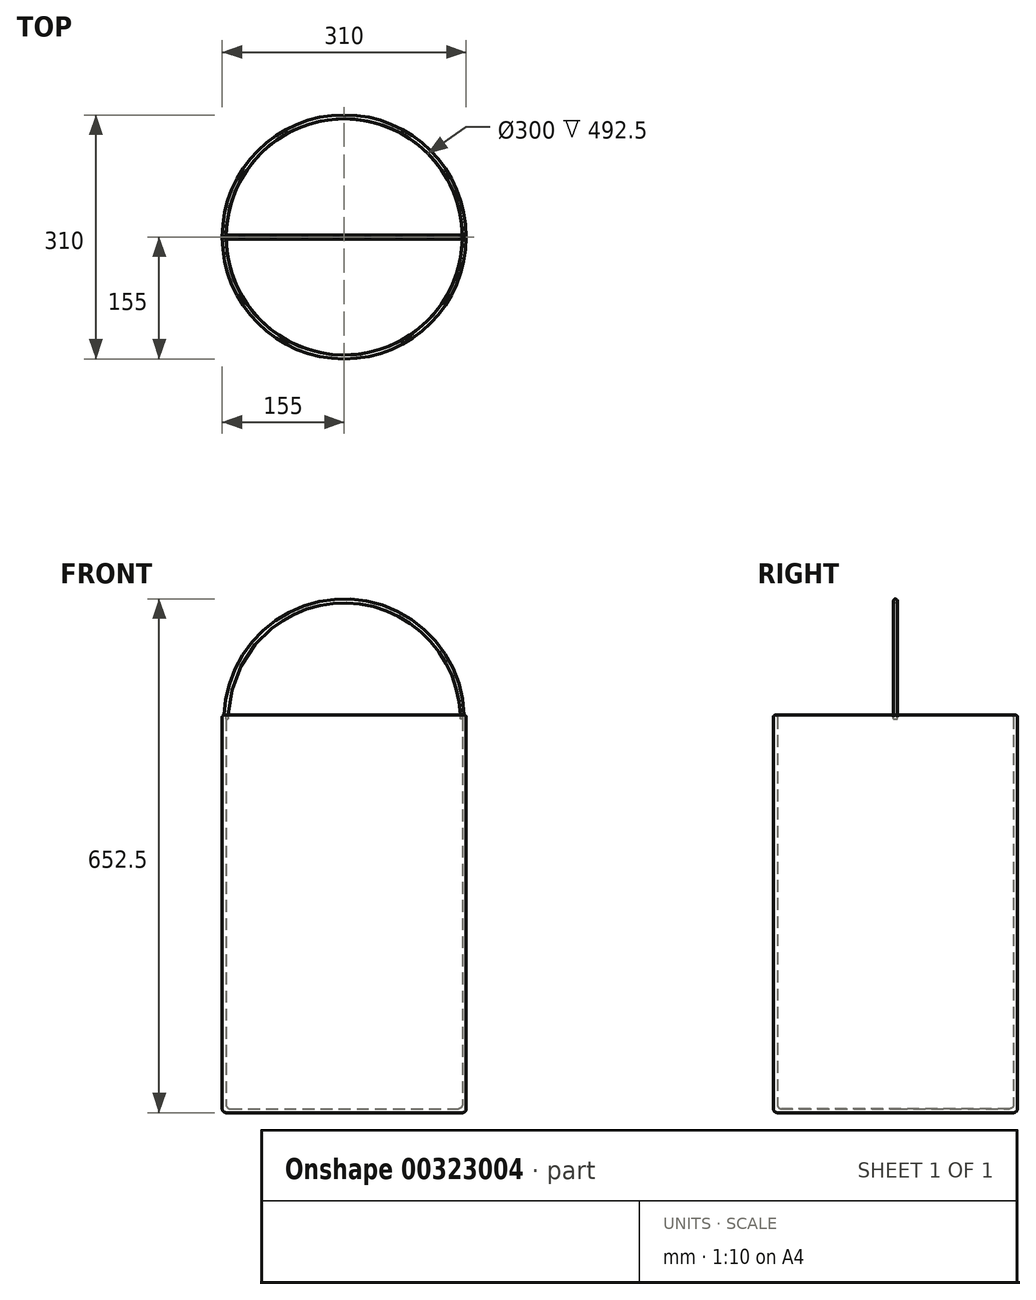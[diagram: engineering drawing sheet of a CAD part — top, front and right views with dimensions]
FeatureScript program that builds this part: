
annotation { "Feature Type Name" : "Feature", "Feature Type Description" : "" }
export const myFeature = defineFeature(function(context is Context, id is Id, definition is map)
    precondition{}
    {
        {
            var Q0;
            Q0=qCreatedBy(makeId("Front.planeOp"),FACE);
            var sketch = newSketch(context, id + "F0", { "sketchPlane" : qUnion([Q0])});
            skLineSegment(sketch, "E0", {"start": v(0, 0) * mm, "end": v(0, 5) * mm});
            skLineSegment(sketch, "E1", {"start": v(0, 0) * mm, "end": v(150, 0) * mm});
            skLineSegment(sketch, "E2", {"start": v(0, 5) * mm, "end": v(145, 5) * mm});
            skLineSegment(sketch, "E3", {"start": v(150, 10) * mm, "end": v(150, 502.5) * mm});
            skLineSegment(sketch, "E4", {"start": v(152.5, 505) * mm, "end": v(152.5, 505) * mm});
            skLineSegment(sketch, "E5", {"start": v(155, 502.5) * mm, "end": v(155, 5) * mm});
            skPoint(sketch, "E6.visualSharp", {"position": v(150, 5) * mm});
            skArc(sketch, "E6.filletArc", {"start": v(145, 5) * mm, "mid": v(148.54, 6.46) * mm, "end": v(150, 10) * mm});
            skPoint(sketch, "E7.visualSharp", {"position": v(155, 0) * mm});
            skArc(sketch, "E7.filletArc", {"start": v(150, 0) * mm, "mid": v(153.54, 1.46) * mm, "end": v(155, 5) * mm});
            skPoint(sketch, "E8.visualSharp", {"position": v(150, 505) * mm});
            skArc(sketch, "E8.filletArc", {"start": v(152.5, 505) * mm, "mid": v(150.73, 504.27) * mm, "end": v(150, 502.5) * mm});
            skPoint(sketch, "E9.visualSharp", {"position": v(155, 505) * mm});
            skArc(sketch, "E9.filletArc", {"start": v(155, 502.5) * mm, "mid": v(154.27, 504.27) * mm, "end": v(152.5, 505) * mm});
            skSolve(sketch);
        }
        {
            var Q0;
            Q0 = qSketchRegion(id + "F0", true);
            var Q1;
            Q1=sQuery(id+"F0.wireOp",EDGE,"E0");
            revolve(context, id + "F1", {"entities" : qUnion([Q0]), "axis" : qUnion([Q1]), "revolveType" : RevolveType.FULL});
        }
        {
            var Q0;
            Q0=qCreatedBy(makeId("Top.planeOp"),FACE);
            cPlane(context, id + "F2", {"entities" : qUnion([Q0]), "cplaneType" : CPlaneType.OFFSET, "offset" : 500 * mm, "width" : 150 * mm, "height" : 150 * mm});
        }
        {
            var Q0;
            Q0=makeQuery(id+"F1.opRevolve","SWEPT_EDGE",EDGE,{"disambiguationData":[OSD([sQuery(id+"F0.wireOp",EDGE,"E3"),sQuery(id+"F0.wireOp",EDGE,"E8.filletArc")])]});
            cPlane(context, id + "F3", {"entities" : qUnion([Q0]), "cplaneType" : CPlaneType.LINE_ANGLE, "offset" : 25 * mm, "angle" : 270 * degree, "width" : 150 * mm, "height" : 150 * mm});
        }
        {
            var Q0;
            Q0=qCreatedBy(id+"F2.planeOp",FACE);
            var sketch = newSketch(context, id + "F4", { "sketchPlane" : qUnion([Q0])});
            skLineSegment(sketch, "E10", {"start": v(0, 0) * mm, "end": v(0, 63.06) * mm});
            skSolve(sketch);
        }
        {
            var Q0;
            Q0=qCreatedBy(id+"F2.planeOp",FACE);
            var sketch = newSketch(context, id + "F5", { "sketchPlane" : qUnion([Q0])});
            skCircle(sketch, "E11", {"center": v(150, 0) * mm, "radius": 2.5 * mm});
            skSolve(sketch);
        }
        {
            var Q0;
            Q0 = qSketchRegion(id + "F5", true);
            var Q1;
            Q1=sQuery(id+"F4.wireOp",EDGE,"E10");
            revolve(context, id + "F6", {"operationType" : NewBodyOperationType.ADD, "entities" : qUnion([Q0]), "axis" : qUnion([Q1]), "revolveType" : RevolveType.ONE_DIRECTION, "oppositeDirection" : true, "angle" : 180 * degree});
        }
    });
